# Revit family: d0067281_REVIT-CONQ 90,100M
name_source: partatom
category: Mechanical Equipment
revit_build: Autodesk Revit 2017 (Build: 20190507_1515(x64)
units: mm (PartAtom-declared; Revit-internal decimal feet)

## family parameters
Always vertical = Yes
Cut with Voids When Loaded = No
Part Type = Normal
Room Calculation Point = No
Round Connector Dimension = Use Radius
Shared = No
Work Plane-Based = No

## types (2) — shared parameters
Air Inlet Radius = 3 5/16"
Air Plenum Extension = 24 7/8"
Apparent Load = 1800 VA
Assembly Code = D3020100
Building Return Extension = 17 13/16"
Building Return Height = 46 1/2"
Building Return NPT = 2"
Building Return Radius = 1"
Burner Body Width = 4 1/16"
Burner Housing Extension = 35"
Burner Housing Height = 17"
Burner Housing Outlet Extension = 29 13/16"
Burner Housing to Left = 7"
Burner Housing to Right = 8"
Center of Burner = 6 3/4"
Cold Inlet Extension = 17 13/16"
Cold Inlet Height = 12"
Cold Inlet NPT = 2"
Cold Inlet Radius = 1"
Combustion Air Connection = 6 5/8"
Combustion Air Connection X = 5 1/2"
Combustion Air Connection Y = 31 1/2"
Combustion Air Extension = 9 3/4"
Combustion Air Inlet Radius = 3 5/16"
Condensate Connection = 3/4"
Condensate Extension = 31 3/4"
Condensate Location = 4"
Condensate Radius = 3/8"
Control Panel Extension = 25 3/16"
Current = 11 A
Description = Conquest® CONDENSING WATER HEATER
Disclaimer = This rendering is for building modeling purposes only. Submittal/catalog is still the contract document. PVI reserves the right to change design and specification without notice.
Drain Angle = -60.00°
Drain Extension = 20 11/16"
Drain Height = 12"
Drain NPT = 1"
Drain Radius = 1/2"
Enclosure Angle = 90.00°
Enclosure Height = 13 3/8"
Enclosure Width = 13 3/8"
Gas Inlet NPT = 1"
Gas Inlet Radius = 1/2"
Gas Train Burner Connection = 26 5/8"
Gas Train Extension = 15"
Gas Train Inlet Height = 13 1/8"
Gas Train Location = 5 1/8"
Gas Train To Rear = 15 3/8"
Height to Bottom of Vent Connection = 3 1/4"
Height to Combustion Air Connection = 87 1/4"
Height to Enclosure = 49 3/4"
Hot Outlet Extension = 17 13/16"
Hot Outlet Height = 67 3/4"
Hot Outlet Location to Left = 10 1/4"
Hot Outlet NPT = 2"
Hot Outlet Radius = 1"
Manufacturer = PVI Industries, LLC
Plenum Location = 5"
Pump Extension = 21 3/16"
Relief Angle = 60.00°
Relief Extension = 20 13/16"
Relief Height = 61 7/8"
Relief NPT = 3/4"
Relief Radius = 3/8"
URL = www.pvi.com
Unit Height = 81"
Unit Radius = 16 13/16"
Vent Angle = 0.00°
Vent Connection = 6 5/8"
Vent Extension = 21 1/2"
Vent Height = 10"
Vent Housing Width = 9 1/2"
Vent Radius = 3 5/16"
Weight = 750

## per-type parameters (varying)
| type | Input | Recovery Rate 40F to 140F (gph) |
| 90 L 130A-GCML | 900000 Btu/h | 1041 |
| 100 L 130A-GCML | 999000 Btu/h | 1157 |

note: column(s) folded — value = type name in every type: Model

## geometry (parser evidence)
native form markers: Sweep x2
no freeform markers — native parametric forms only
